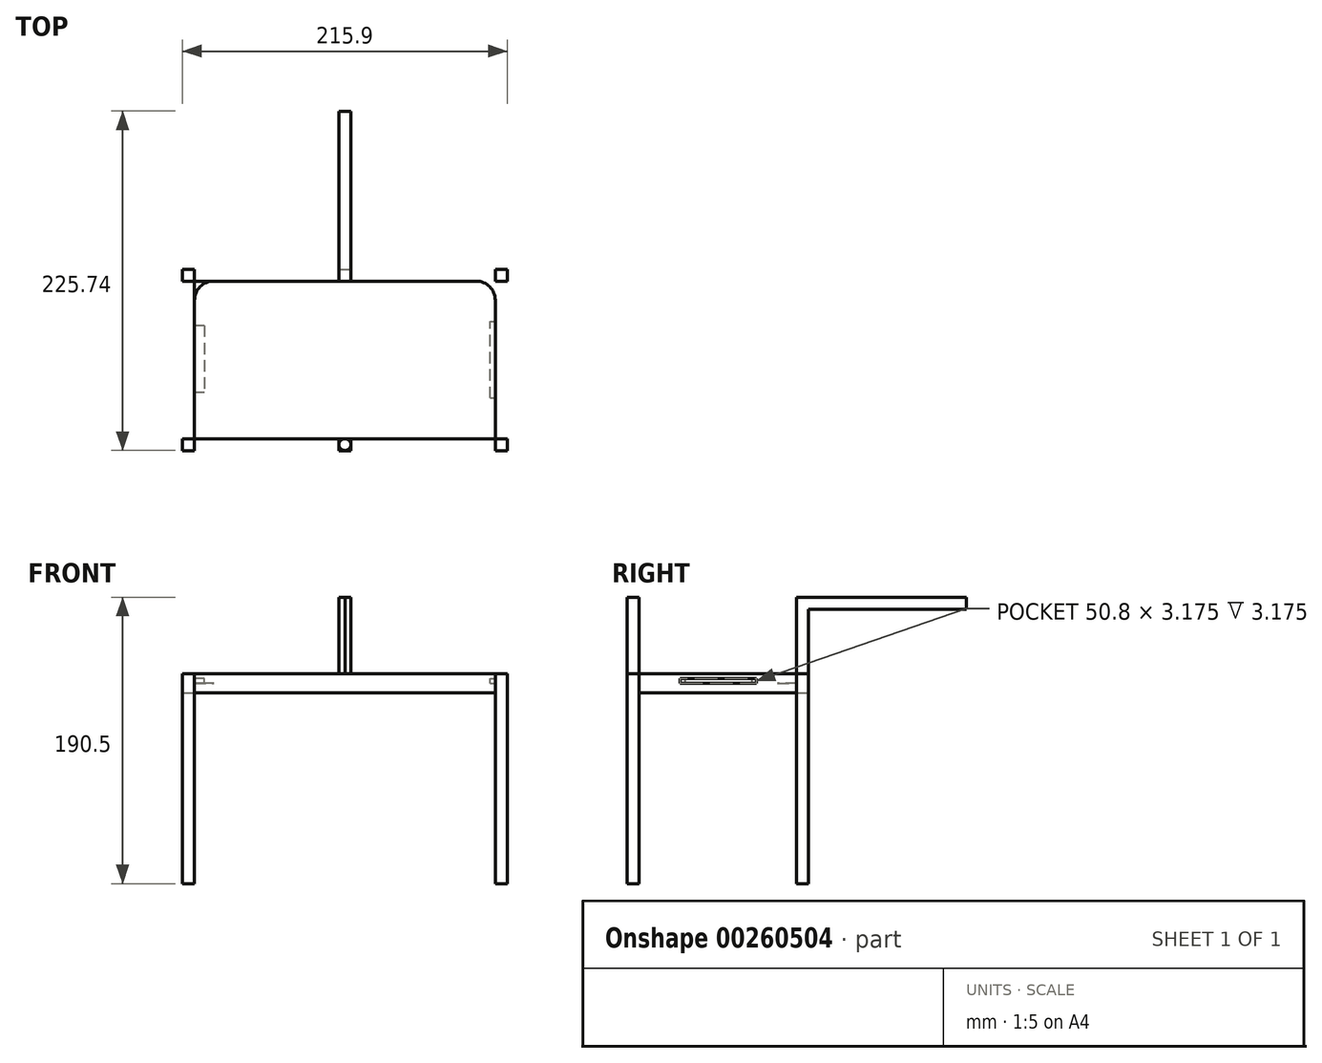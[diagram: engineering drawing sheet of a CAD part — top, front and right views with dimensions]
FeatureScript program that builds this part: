
annotation { "Feature Type Name" : "Feature", "Feature Type Description" : "" }
export const myFeature = defineFeature(function(context is Context, id is Id, definition is map)
    precondition{}
    {
        {
            var Q0;
            Q0=qCreatedBy(makeId("Top.planeOp"),FACE);
            var sketch = newSketch(context, id + "F0", { "sketchPlane" : qUnion([Q0])});
            skLineSegment(sketch, "E0.bottom", {"start": v(-107.95, -60.33) * mm, "end": v(107.95, -60.33) * mm});
            skLineSegment(sketch, "E0.top", {"start": v(-107.95, 60.33) * mm, "end": v(107.95, 60.33) * mm});
            skLineSegment(sketch, "E0.left", {"start": v(-107.95, -60.33) * mm, "end": v(-107.95, 60.33) * mm});
            skLineSegment(sketch, "E0.right", {"start": v(107.95, -60.33) * mm, "end": v(107.95, 60.33) * mm});
            skPoint(sketch, "E0.middle", {"position": v(0, 0) * mm});
            skLineSegment(sketch, "E1.bottom", {"start": v(-100.01, -52.39) * mm, "end": v(100.01, -52.39) * mm});
            skLineSegment(sketch, "E1.top", {"start": v(-100.01, 52.39) * mm, "end": v(100.01, 52.39) * mm});
            skLineSegment(sketch, "E1.left", {"start": v(-100.01, -52.39) * mm, "end": v(-100.01, 52.39) * mm});
            skLineSegment(sketch, "E1.right", {"start": v(100.01, -52.39) * mm, "end": v(100.01, 52.39) * mm});
            skPoint(sketch, "E2", {"position": v(-87.31, 39.69) * mm});
            skPoint(sketch, "E3", {"position": v(87.31, 39.69) * mm});
            skPoint(sketch, "E4", {"position": v(87.31, -39.69) * mm});
            skPoint(sketch, "E5", {"position": v(-87.31, -39.69) * mm});
            skArc(sketch, "E6", {"start": v(-100.01, 39.69) * mm, "mid": v(-96.3, 48.67) * mm, "end": v(-87.31, 52.39) * mm});
            skArc(sketch, "E7", {"start": v(87.31, 52.39) * mm, "mid": v(96.3, 48.67) * mm, "end": v(100.01, 39.69) * mm});
            skArc(sketch, "E8", {"start": v(87.31, -52.39) * mm, "mid": v(96.3, -48.67) * mm, "end": v(100.01, -39.69) * mm});
            skArc(sketch, "E9", {"start": v(-100.01, -39.69) * mm, "mid": v(-96.3, -48.67) * mm, "end": v(-87.31, -52.39) * mm});
            skLineSegment(sketch, "E10.bottom", {"start": v(-100.01, -52.39) * mm, "end": v(-107.95, -52.39) * mm});
            skLineSegment(sketch, "E10.top", {"start": v(-100.01, -60.33) * mm, "end": v(-107.95, -60.33) * mm});
            skLineSegment(sketch, "E10.left", {"start": v(-100.01, -52.39) * mm, "end": v(-100.01, -60.33) * mm});
            skLineSegment(sketch, "E10.right", {"start": v(-107.95, -52.39) * mm, "end": v(-107.95, -60.33) * mm});
            skLineSegment(sketch, "E11.bottom", {"start": v(-107.95, 60.33) * mm, "end": v(-100.01, 60.33) * mm});
            skLineSegment(sketch, "E11.top", {"start": v(-107.95, 52.39) * mm, "end": v(-100.01, 52.39) * mm});
            skLineSegment(sketch, "E11.left", {"start": v(-107.95, 60.33) * mm, "end": v(-107.95, 52.39) * mm});
            skLineSegment(sketch, "E11.right", {"start": v(-100.01, 60.33) * mm, "end": v(-100.01, 52.39) * mm});
            skLineSegment(sketch, "E12.bottom", {"start": v(100.01, 52.39) * mm, "end": v(107.95, 52.39) * mm});
            skLineSegment(sketch, "E12.top", {"start": v(100.01, 60.33) * mm, "end": v(107.95, 60.33) * mm});
            skLineSegment(sketch, "E12.left", {"start": v(100.01, 52.39) * mm, "end": v(100.01, 60.33) * mm});
            skLineSegment(sketch, "E12.right", {"start": v(107.95, 52.39) * mm, "end": v(107.95, 60.33) * mm});
            skLineSegment(sketch, "E13.bottom", {"start": v(100.01, -52.39) * mm, "end": v(107.95, -52.39) * mm});
            skLineSegment(sketch, "E13.top", {"start": v(100.01, -60.33) * mm, "end": v(107.95, -60.33) * mm});
            skLineSegment(sketch, "E13.left", {"start": v(100.01, -52.39) * mm, "end": v(100.01, -60.33) * mm});
            skLineSegment(sketch, "E13.right", {"start": v(107.95, -52.39) * mm, "end": v(107.95, -60.33) * mm});
            skSolve(sketch);
        }
        {
            var Q0;
            {var subQ3=sQuery(id+"F0.wireOp",EDGE,"E6");Q0=makeQuery(id+"F0.imprint","IMPRINT",FACE,{"disambiguationData":[TD([[makeQuery(id+"F0.imprint","IMPRINT",EDGE,{"derivedFrom":subQ3}),-1.0]])]});}
            extrude(context, id + "F1", {"entities" : qUnion([Q0]), "depth" : 6.35 * mm});
        }
        {
            var Q0;
            {var subQ3=sQuery(id+"F0.wireOp",EDGE,"E9");Q0=makeQuery(id+"F0.imprint","IMPRINT",FACE,{"disambiguationData":[TD([[makeQuery(id+"F0.imprint","IMPRINT",EDGE,{"derivedFrom":subQ3}),-1.0]])]});}
            var Q1;
            Q1=makeQuery(id+"F0.imprint","IMPRINT",FACE,{"disambiguationData":[TD([[makeQuery(id+"F0.imprint","IMPRINT",EDGE,{"derivedFrom":sQuery(id+"F0.wireOp",EDGE,"E0.left")}),-1.0]])]});
            var Q2;
            Q2=makeQuery(id+"F0.imprint","IMPRINT",FACE,{"disambiguationData":[TD([[makeQuery(id+"F0.imprint","IMPRINT",EDGE,{"derivedFrom":sQuery(id+"F0.wireOp",EDGE,"E0.bottom")}),1.0]])]});
            var Q3;
            Q3=makeQuery(id+"F0.imprint","IMPRINT",FACE,{"disambiguationData":[TD([[makeQuery(id+"F0.imprint","IMPRINT",EDGE,{"derivedFrom":sQuery(id+"F0.wireOp",EDGE,"E0.top")}),-1.0]])]});
            var Q4;
            {var subQ3=sQuery(id+"F0.wireOp",EDGE,"E6");Q4=makeQuery(id+"F0.imprint","IMPRINT",FACE,{"disambiguationData":[TD([[makeQuery(id+"F0.imprint","IMPRINT",EDGE,{"derivedFrom":subQ3}),1.0]])]});}
            var Q5;
            {var subQ3=sQuery(id+"F0.wireOp",EDGE,"E7");Q5=makeQuery(id+"F0.imprint","IMPRINT",FACE,{"disambiguationData":[TD([[makeQuery(id+"F0.imprint","IMPRINT",EDGE,{"derivedFrom":subQ3}),1.0]])]});}
            var Q6;
            Q6=makeQuery(id+"F0.imprint","IMPRINT",FACE,{"disambiguationData":[TD([[makeQuery(id+"F0.imprint","IMPRINT",EDGE,{"derivedFrom":sQuery(id+"F0.wireOp",EDGE,"E0.right")}),1.0]])]});
            var Q7;
            {var subQ3=sQuery(id+"F0.wireOp",EDGE,"E8");Q7=makeQuery(id+"F0.imprint","IMPRINT",FACE,{"disambiguationData":[TD([[makeQuery(id+"F0.imprint","IMPRINT",EDGE,{"derivedFrom":subQ3}),-1.0]])]});}
            var Q8;
            Q8=makeQuery(id+"F0.imprint","IMPRINT",FACE,{"disambiguationData":[TD([[makeQuery(id+"F0.imprint","IMPRINT",EDGE,{"derivedFrom":sQuery(id+"F0.wireOp",EDGE,"E13.bottom")}),-1.0]])]});
            var Q9;
            Q9=makeQuery(id+"F0.imprint","IMPRINT",FACE,{"disambiguationData":[TD([[makeQuery(id+"F0.imprint","IMPRINT",EDGE,{"derivedFrom":sQuery(id+"F0.wireOp",EDGE,"E12.bottom")}),1.0]])]});
            var Q10;
            Q10=makeQuery(id+"F0.imprint","IMPRINT",FACE,{"disambiguationData":[TD([[makeQuery(id+"F0.imprint","IMPRINT",EDGE,{"derivedFrom":sQuery(id+"F0.wireOp",EDGE,"E11.bottom")}),-1.0]])]});
            var Q11;
            Q11=makeQuery(id+"F0.imprint","IMPRINT",FACE,{"disambiguationData":[TD([[makeQuery(id+"F0.imprint","IMPRINT",EDGE,{"derivedFrom":sQuery(id+"F0.wireOp",EDGE,"E10.bottom")}),1.0]])]});
            extrude(context, id + "F2", {"entities" : qUnion([Q0, Q1, Q2, Q3, Q4, Q5, Q6, Q7, Q8, Q9, Q10, Q11]), "operationType" : NewBodyOperationType.ADD, "depth" : 12.7 * mm});
        }
        {
            var Q0;
            Q0=makeQuery(id+"F0.imprint","IMPRINT",FACE,{"disambiguationData":[TD([[makeQuery(id+"F0.imprint","IMPRINT",EDGE,{"derivedFrom":sQuery(id+"F0.wireOp",EDGE,"E10.bottom")}),1.0]])]});
            var Q1;
            Q1=makeQuery(id+"F0.imprint","IMPRINT",FACE,{"disambiguationData":[TD([[makeQuery(id+"F0.imprint","IMPRINT",EDGE,{"derivedFrom":sQuery(id+"F0.wireOp",EDGE,"E11.bottom")}),-1.0]])]});
            var Q2;
            Q2=makeQuery(id+"F0.imprint","IMPRINT",FACE,{"disambiguationData":[TD([[makeQuery(id+"F0.imprint","IMPRINT",EDGE,{"derivedFrom":sQuery(id+"F0.wireOp",EDGE,"E12.bottom")}),1.0]])]});
            var Q3;
            Q3=makeQuery(id+"F0.imprint","IMPRINT",FACE,{"disambiguationData":[TD([[makeQuery(id+"F0.imprint","IMPRINT",EDGE,{"derivedFrom":sQuery(id+"F0.wireOp",EDGE,"E13.bottom")}),-1.0]])]});
            extrude(context, id + "F3", {"entities" : qUnion([Q0, Q1, Q2, Q3]), "operationType" : NewBodyOperationType.ADD, "oppositeDirection" : true, "depth" : 127 * mm});
        }
        {
            var Q0;
            Q0=makeQuery(id+"F2.opExtrude","CAP_FACE",FACE,{"disambiguationData":[OSD([sQuery(id+"F0.wireOp",EDGE,"E0.bottom"),sQuery(id+"F0.wireOp",EDGE,"E0.top"),sQuery(id+"F0.wireOp",EDGE,"E0.left"),sQuery(id+"F0.wireOp",EDGE,"E0.right"),sQuery(id+"F0.wireOp",EDGE,"E1.bottom"),sQuery(id+"F0.wireOp",EDGE,"E1.top"),sQuery(id+"F0.wireOp",EDGE,"E1.left"),sQuery(id+"F0.wireOp",EDGE,"E1.right"),sQuery(id+"F0.wireOp",EDGE,"E6"),sQuery(id+"F0.wireOp",EDGE,"E7"),sQuery(id+"F0.wireOp",EDGE,"E8"),sQuery(id+"F0.wireOp",EDGE,"E9"),sQuery(id+"F0.wireOp",EDGE,"E10.top"),sQuery(id+"F0.wireOp",EDGE,"E10.right"),sQuery(id+"F0.wireOp",EDGE,"E11.bottom"),sQuery(id+"F0.wireOp",EDGE,"E11.left"),sQuery(id+"F0.wireOp",EDGE,"E12.top"),sQuery(id+"F0.wireOp",EDGE,"E12.right"),sQuery(id+"F0.wireOp",EDGE,"E13.top"),sQuery(id+"F0.wireOp",EDGE,"E13.right")])],"isStart":false});
            var sketch = newSketch(context, id + "F4", { "sketchPlane" : qUnion([Q0])});
            skLineSegment(sketch, "E14", {"start": v(0, -60.33) * mm, "end": v(0, -52.39) * mm});
            skLineSegment(sketch, "E15", {"start": v(0, 52.39) * mm, "end": v(0, 60.33) * mm});
            skCircle(sketch, "E16", {"center": v(0, -56.36) * mm, "radius": 3.97 * mm});
            skCircle(sketch, "E17", {"center": v(0, 56.36) * mm, "radius": 3.97 * mm});
            skLineSegment(sketch, "E18.bottom", {"start": v(-3.98, 52.39) * mm, "end": v(3.98, 52.39) * mm});
            skLineSegment(sketch, "E18.top", {"start": v(-3.98, 60.33) * mm, "end": v(3.98, 60.33) * mm});
            skLineSegment(sketch, "E18.left", {"start": v(-3.98, 52.39) * mm, "end": v(-3.98, 60.33) * mm});
            skLineSegment(sketch, "E18.right", {"start": v(3.98, 52.39) * mm, "end": v(3.98, 60.33) * mm});
            skLineSegment(sketch, "E19.bottom", {"start": v(0, -52.39) * mm, "end": v(0, -52.39) * mm});
            skLineSegment(sketch, "E19.top", {"start": v(0, -60.33) * mm, "end": v(0, -60.33) * mm});
            skLineSegment(sketch, "E19.left", {"start": v(0, -52.39) * mm, "end": v(0, -60.33) * mm});
            skLineSegment(sketch, "E19.right", {"start": v(0, -52.39) * mm, "end": v(0, -60.33) * mm});
            skLineSegment(sketch, "E20.bottom", {"start": v(-3.98, -52.39) * mm, "end": v(3.98, -52.39) * mm});
            skLineSegment(sketch, "E20.top", {"start": v(-3.98, -60.33) * mm, "end": v(3.98, -60.33) * mm});
            skLineSegment(sketch, "E20.left", {"start": v(-3.98, -52.39) * mm, "end": v(-3.98, -60.33) * mm});
            skLineSegment(sketch, "E20.right", {"start": v(3.98, -52.39) * mm, "end": v(3.98, -60.33) * mm});
            skSolve(sketch);
        }
        {
            var Q0;
            {var subQ0=sQuery(id+"F4.wireOp",EDGE,"E15");Q0=makeQuery(id+"F4.imprint","IMPRINT",FACE,{"disambiguationData":[TD([[makeQuery(id+"F4.imprint","IMPRINT",EDGE,{"derivedFrom":subQ0}),1.0]])]});}
            var Q1;
            {var subQ0=sQuery(id+"F4.wireOp",EDGE,"E19.right");Q1=makeQuery(id+"F4.imprint","IMPRINT",FACE,{"disambiguationData":[TD([[makeQuery(id+"F4.imprint","IMPRINT",EDGE,{"derivedFrom":subQ0}),-1.0]])]});}
            var Q2;
            {var subQ0=sQuery(id+"F4.wireOp",EDGE,"E19.right");Q2=makeQuery(id+"F4.imprint","IMPRINT",FACE,{"disambiguationData":[TD([[makeQuery(id+"F4.imprint","IMPRINT",EDGE,{"derivedFrom":subQ0}),1.0]])]});}
            var Q3;
            {var subQ6=sQuery(id+"F4.wireOp",EDGE,"E20.left");Q3=makeQuery(id+"F4.imprint","IMPRINT",FACE,{"disambiguationData":[TD([[makeQuery(id+"F4.imprint","IMPRINT",EDGE,{"derivedFrom":subQ6}),1.0]])]});}
            var Q4;
            {var subQ6=sQuery(id+"F4.wireOp",EDGE,"E20.right");Q4=makeQuery(id+"F4.imprint","IMPRINT",FACE,{"disambiguationData":[TD([[makeQuery(id+"F4.imprint","IMPRINT",EDGE,{"derivedFrom":subQ6}),-1.0]])]});}
            var Q5;
            {var subQ6=sQuery(id+"F4.wireOp",EDGE,"E18.right");Q5=makeQuery(id+"F4.imprint","IMPRINT",FACE,{"disambiguationData":[TD([[makeQuery(id+"F4.imprint","IMPRINT",EDGE,{"derivedFrom":subQ6}),1.0]])]});}
            var Q6;
            {var subQ0=sQuery(id+"F4.wireOp",EDGE,"E15");Q6=makeQuery(id+"F4.imprint","IMPRINT",FACE,{"disambiguationData":[TD([[makeQuery(id+"F4.imprint","IMPRINT",EDGE,{"derivedFrom":subQ0}),-1.0]])]});}
            var Q7;
            {var subQ6=sQuery(id+"F4.wireOp",EDGE,"E18.left");Q7=makeQuery(id+"F4.imprint","IMPRINT",FACE,{"disambiguationData":[TD([[makeQuery(id+"F4.imprint","IMPRINT",EDGE,{"derivedFrom":subQ6}),-1.0]])]});}
            extrude(context, id + "F5", {"entities" : qUnion([Q0, Q1, Q2, Q3, Q4, Q5, Q6, Q7]), "operationType" : NewBodyOperationType.ADD, "depth" : 50.8 * mm});
        }
        {
            var Q0;
            Q0=makeQuery(id+"F5.boolean.opBoolean","MERGE",FACE,{"derivedFrom":[makeQuery(id+"F2.opExtrude","SWEPT_FACE",FACE,{"disambiguationData":[OSD([sQuery(id+"F0.wireOp",EDGE,"E1.top")])]}),makeQuery(id+"F5.opExtrude","SWEPT_FACE",FACE,{"disambiguationData":[OSD([sQuery(id+"F4.wireOp",EDGE,"E18.bottom")])]})]});
            var sketch = newSketch(context, id + "F6", { "sketchPlane" : qUnion([Q0])});
            skLineSegment(sketch, "E21.bottom", {"start": v(-3.98, 63.5) * mm, "end": v(3.98, 63.5) * mm});
            skLineSegment(sketch, "E21.top", {"start": v(-3.98, 55.55) * mm, "end": v(3.98, 55.55) * mm});
            skLineSegment(sketch, "E21.left", {"start": v(-3.98, 63.5) * mm, "end": v(-3.98, 55.55) * mm});
            skLineSegment(sketch, "E21.right", {"start": v(3.98, 63.5) * mm, "end": v(3.98, 55.55) * mm});
            skPoint(sketch, "E21.middle", {"position": v(0, 59.52) * mm});
            skSolve(sketch);
        }
        {
            var Q0;
            Q0 = qSketchRegion(id + "F6", true);
            extrude(context, id + "F7", {"entities" : qUnion([Q0]), "operationType" : NewBodyOperationType.ADD, "depth" : 113.03 * mm});
        }
        {
            var Q0;
            Q0=makeQuery(id+"F2.opExtrude","SWEPT_FACE",FACE,{"disambiguationData":[OSD([sQuery(id+"F0.wireOp",EDGE,"E1.left")])]});
            var sketch = newSketch(context, id + "F8", { "sketchPlane" : qUnion([Q0])});
            skLineSegment(sketch, "E22.left", {"start": v(-22.76, 0) * mm, "end": v(-22.76, 9.53) * mm});
            skLineSegment(sketch, "E22.right", {"start": v(21.69, 0) * mm, "end": v(21.69, 6.35) * mm});
            skLineSegment(sketch, "E23.bottom", {"start": v(-22.76, 9.53) * mm, "end": v(21.69, 9.53) * mm});
            skLineSegment(sketch, "E23.top", {"start": v(-22.76, 6.35) * mm, "end": v(21.69, 6.35) * mm});
            skLineSegment(sketch, "E23.left", {"start": v(-22.76, 6.35) * mm, "end": v(-22.76, 9.53) * mm});
            skLineSegment(sketch, "E23.right", {"start": v(21.69, 6.35) * mm, "end": v(21.69, 9.53) * mm});
            skLineSegment(sketch, "E24.top", {"start": v(-22.76, 12.7) * mm, "end": v(21.69, 12.7) * mm});
            skLineSegment(sketch, "E24.left", {"start": v(-22.76, 9.53) * mm, "end": v(-22.76, 12.7) * mm});
            skLineSegment(sketch, "E24.right", {"start": v(21.69, 9.53) * mm, "end": v(21.69, 12.7) * mm});
            skSolve(sketch);
        }
        {
            var Q0;
            Q0=makeQuery(id+"F8.imprint","IMPRINT",FACE,{"disambiguationData":[TD([[makeQuery(id+"F8.imprint","IMPRINT",EDGE,{"derivedFrom":sQuery(id+"F8.wireOp",EDGE,"E23.top")}),1.0]])]});
            extrude(context, id + "F9", {"entities" : qUnion([Q0]), "operationType" : NewBodyOperationType.REMOVE, "oppositeDirection" : true, "depth" : 6.35 * mm});
        }
        {
            var Q0;
            Q0=makeQuery(id+"F2.opExtrude","SWEPT_FACE",FACE,{"disambiguationData":[OSD([sQuery(id+"F0.wireOp",EDGE,"E1.right")])]});
            var sketch = newSketch(context, id + "F10", { "sketchPlane" : qUnion([Q0])});
            skLineSegment(sketch, "E25.bottom", {"start": v(-25.32, 6.35) * mm, "end": v(25.48, 6.35) * mm});
            skLineSegment(sketch, "E25.top", {"start": v(-25.32, 9.53) * mm, "end": v(25.48, 9.53) * mm});
            skLineSegment(sketch, "E25.left", {"start": v(-25.32, 6.35) * mm, "end": v(-25.32, 9.53) * mm});
            skLineSegment(sketch, "E25.right", {"start": v(25.48, 6.35) * mm, "end": v(25.48, 9.53) * mm});
            skSolve(sketch);
        }
        {
            var Q0;
            Q0 = qSketchRegion(id + "F10", true);
            extrude(context, id + "F11", {"entities" : qUnion([Q0]), "operationType" : NewBodyOperationType.REMOVE, "oppositeDirection" : true, "depth" : 3.17 * mm});
        }
    });
